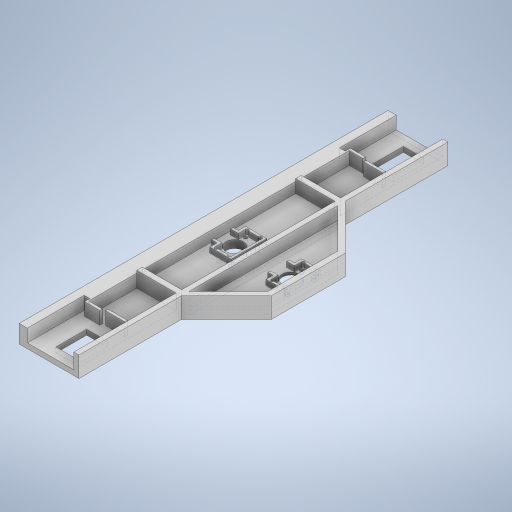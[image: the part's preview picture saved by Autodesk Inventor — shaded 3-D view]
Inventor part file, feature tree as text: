
AUTODESK INVENTOR PART (.ipt)
format: ipt  version: 2024 (Build 280153000, 153)  size: 551,936 bytes
history: native  units: mm
features: sketch x13, extrude x12, projected_geometry x3, chamfer x2, other x1
ambient origin geometry x8: Origin, YZ Plane, XZ Plane, XY Plane, X Axis, Y Axis, Z Axis, Center Point
bodies: Body1 (feature_tree)
feature tree (31):
  other  "Твердое тело1"
  extrude  "Выдавливание1"  Depth=722.0mm
  extrude  "Выдавливание2"  Depth=21.0mm
  extrude  "Выдавливание3"  Depth=60.0mm
  extrude  "Выдавливание4"  Depth=40.0mm
  extrude  "Выдавливание5"  Depth=10.0mm TaperAngle=0.0deg
  extrude  "Выдавливание6"  Depth=10.0mm
  extrude  "Выдавливание7"  Depth=500.0mm
  extrude  "Выдавливание8"  Depth=111.0mm
  chamfer  "Фаска1"  Distance=25.0mm
  extrude  "Выдавливание9"  Depth=722.0mm
  extrude  "Выдавливание11"  TaperAngle=0.0deg  [1 undecoded]
  sketch  "Sketch13"  dims[d0=87.0mm d1=722.0mm]
  chamfer  "Chamfer2"  Distance=35.0mm
  extrude  "Extrusion12"  Depth=20.0mm
  extrude  "Extrusion13"  Depth=10.0mm
  sketch  "Эскиз1"
  sketch  "Эскиз2"
  sketch  "Эскиз3"
  sketch  "Эскиз4"
  sketch  "Эскиз6"
  sketch  "Эскиз7"
  sketch  "Эскиз8"
  sketch  "Эскиз9"
  projected_geometry  "Спроецированная петля1"
  sketch  "Эскиз10"
  projected_geometry  "Спроецированная петля2"
  projected_geometry  "Спроецированная петля3"
  sketch  "Эскиз12"
  sketch  "Sketch14"  dims[d2=10.0mm d3=0.0mm d4=21.0mm]
  sketch  "Sketch15"  dims[d5=16.0mm d6=60.0mm d7=40.0mm d8=10.0mm d9=0.0mm d10=10.0mm d12=500.0mm d13=111.0mm d14=25.0mm d15=0.0mm d16=722.0mm d17=0.0mm d18=35.0mm d19=0.0mm d20=20.0mm d22=10.0mm d23=40.0mm d24=0.0mm d25=200.0mm d26=200.0mm d27=5.0mm d28=0.0mm d29=42.0mm d30=70.0mm d31=326.0mm d32=5.0mm d33=10.5mm d34=10.0mm d35=0.0mm d36=4.25mm d37=4.25mm d38=4.25mm d39=4.25mm d40=19.0mm d41=34.0mm d42=20.0mm d43=0.0mm d44=12.0mm d45=2.0mm d46=45.0deg d47=5.0mm d48=5.0mm d49=19.0mm d50=19.0mm d51=2.0mm d52=0.0mm d56=10.0mm d57=20.0mm d58=5.0mm d59=25.0mm d60=0.0mm d61=42.0mm d62=70.0mm d63=5.0mm d64=10.5mm d65=5.0mm d66=5.0mm d67=19.0mm d68=19.0mm d69=19.0mm d70=34.0mm d71=88.0mm d72=2.0mm d73=45.0deg d75=11.0mm d76=40.0mm d77=0.0mm d78=11.0mm d79=11.0mm d80=2.0mm d81=0.0mm]
note: 1 required parameter value undecoded (feature->parameter linkage not recoverable at this tier; creation-order binding heuristic only, values carry confidence <= 0.55)
